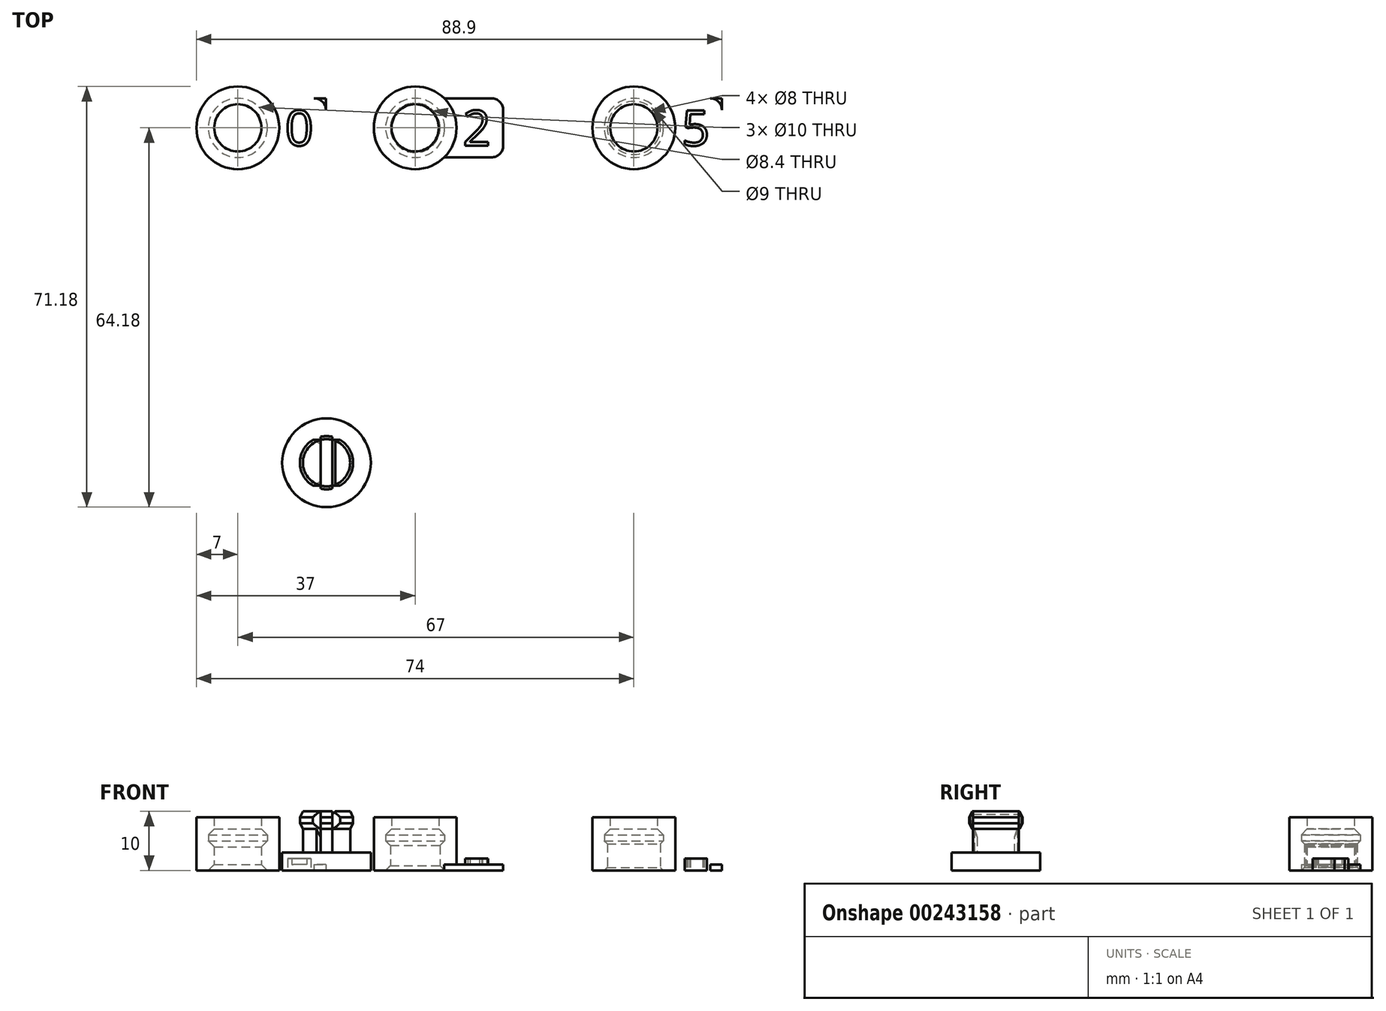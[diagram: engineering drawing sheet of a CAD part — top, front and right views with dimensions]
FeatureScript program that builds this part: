
annotation { "Feature Type Name" : "Feature", "Feature Type Description" : "" }
export const myFeature = defineFeature(function(context is Context, id is Id, definition is map)
    precondition{}
    {
        {
            var Q0;
            Q0=qCreatedBy(makeId("Front.planeOp"),FACE);
            var sketch = newSketch(context, id + "F0", { "sketchPlane" : qUnion([Q0])});
            skLineSegment(sketch, "E0", {"start": v(0, 0) * mm, "end": v(0, 7) * mm, "construction": true});
            skLineSegment(sketch, "E1", {"start": v(0, 7) * mm, "end": v(0, 9) * mm, "construction": true});
            skLineSegment(sketch, "E2", {"start": v(0, 9) * mm, "end": v(-4, 9) * mm, "construction": true});
            skLineSegment(sketch, "E3", {"start": v(0, 0) * mm, "end": v(-4, 0) * mm, "construction": true});
            skLineSegment(sketch, "E4", {"start": v(-4, 9) * mm, "end": v(-4, 7) * mm});
            skLineSegment(sketch, "E5", {"start": v(-4, 7) * mm, "end": v(-5, 6) * mm});
            skLineSegment(sketch, "E6", {"start": v(-5, 6) * mm, "end": v(-5, 5) * mm});
            skLineSegment(sketch, "E7", {"start": v(-5, 5) * mm, "end": v(-4, 4) * mm});
            skLineSegment(sketch, "E8", {"start": v(-4, 4) * mm, "end": v(-4, 0) * mm});
            skLineSegment(sketch, "E9", {"start": v(-4, 0) * mm, "end": v(-7, 0) * mm});
            skLineSegment(sketch, "E10", {"start": v(-7, 0) * mm, "end": v(-7, 9) * mm});
            skLineSegment(sketch, "E11", {"start": v(-7, 9) * mm, "end": v(-4, 9) * mm});
            skLineSegment(sketch, "E12", {"start": v(-4, 1) * mm, "end": v(-5, 0) * mm});
            skLineSegment(sketch, "E13", {"start": v(30, 0) * mm, "end": v(30, 7) * mm, "construction": true});
            skLineSegment(sketch, "E14", {"start": v(30, 7) * mm, "end": v(30, 9) * mm, "construction": true});
            skLineSegment(sketch, "E15", {"start": v(30, 9) * mm, "end": v(26, 9) * mm, "construction": true});
            skLineSegment(sketch, "E16", {"start": v(30, 0) * mm, "end": v(25.8, 0) * mm, "construction": true});
            skLineSegment(sketch, "E17", {"start": v(26, 9) * mm, "end": v(26, 7) * mm});
            skLineSegment(sketch, "E18", {"start": v(26, 7) * mm, "end": v(25, 6) * mm});
            skLineSegment(sketch, "E19", {"start": v(25, 6) * mm, "end": v(25, 5) * mm});
            skLineSegment(sketch, "E20", {"start": v(25, 5) * mm, "end": v(25.8, 4.2) * mm});
            skLineSegment(sketch, "E21", {"start": v(25.8, 4.2) * mm, "end": v(25.8, 0) * mm});
            skLineSegment(sketch, "E22", {"start": v(25.8, 0) * mm, "end": v(23, 0) * mm});
            skLineSegment(sketch, "E23", {"start": v(23, 0) * mm, "end": v(23, 9) * mm});
            skLineSegment(sketch, "E24", {"start": v(23, 9) * mm, "end": v(26, 9) * mm});
            skLineSegment(sketch, "E25", {"start": v(25.8, 0.8) * mm, "end": v(25, 0) * mm});
            skLineSegment(sketch, "E26", {"start": v(67, 0) * mm, "end": v(67, 7) * mm, "construction": true});
            skLineSegment(sketch, "E27", {"start": v(67, 7) * mm, "end": v(67, 9) * mm, "construction": true});
            skLineSegment(sketch, "E28", {"start": v(67, 9) * mm, "end": v(63, 9) * mm, "construction": true});
            skLineSegment(sketch, "E29", {"start": v(67, 0) * mm, "end": v(62.5, 0) * mm, "construction": true});
            skLineSegment(sketch, "E30", {"start": v(63, 9) * mm, "end": v(63, 7) * mm});
            skLineSegment(sketch, "E31", {"start": v(63, 7) * mm, "end": v(62, 6) * mm});
            skLineSegment(sketch, "E32", {"start": v(62, 6) * mm, "end": v(62, 5) * mm});
            skLineSegment(sketch, "E33", {"start": v(62, 5) * mm, "end": v(62.5, 4.5) * mm});
            skLineSegment(sketch, "E34", {"start": v(62.5, 4.5) * mm, "end": v(62.5, 0) * mm});
            skLineSegment(sketch, "E35", {"start": v(62.5, 0) * mm, "end": v(60, 0) * mm});
            skLineSegment(sketch, "E36", {"start": v(60, 0) * mm, "end": v(60, 9) * mm});
            skLineSegment(sketch, "E37", {"start": v(60, 9) * mm, "end": v(63, 9) * mm});
            skLineSegment(sketch, "E38", {"start": v(62.5, 0.5) * mm, "end": v(62, 0) * mm});
            skSolve(sketch);
        }
        {
            var Q0;
            Q0=makeQuery(id+"F0.imprint","IMPRINT",FACE,{"disambiguationData":[TD([[makeQuery(id+"F0.imprint","IMPRINT",EDGE,{"derivedFrom":sQuery(id+"F0.wireOp",EDGE,"E4")}),-1.0]])]});
            var Q1;
            Q1=sQuery(id+"F0.wireOp",EDGE,"E0");
            revolve(context, id + "F1", {"entities" : qUnion([Q0]), "axis" : qUnion([Q1]), "revolveType" : RevolveType.FULL});
        }
        {
            var Q0;
            Q0=makeQuery(id+"F0.imprint","IMPRINT",FACE,{"disambiguationData":[TD([[makeQuery(id+"F0.imprint","IMPRINT",EDGE,{"derivedFrom":sQuery(id+"F0.wireOp",EDGE,"E17")}),-1.0]])]});
            var Q1;
            Q1=sQuery(id+"F0.wireOp",EDGE,"E13");
            revolve(context, id + "F2", {"entities" : qUnion([Q0]), "axis" : qUnion([Q1]), "revolveType" : RevolveType.FULL});
        }
        {
            var Q0;
            Q0=makeQuery(id+"F0.imprint","IMPRINT",FACE,{"disambiguationData":[TD([[makeQuery(id+"F0.imprint","IMPRINT",EDGE,{"derivedFrom":sQuery(id+"F0.wireOp",EDGE,"E30")}),-1.0]])]});
            var Q1;
            Q1=sQuery(id+"F0.wireOp",EDGE,"E26");
            revolve(context, id + "F3", {"entities" : qUnion([Q0]), "axis" : qUnion([Q1]), "revolveType" : RevolveType.FULL});
        }
        {
            var Q0;
            Q0=qCreatedBy(makeId("Top.planeOp"),FACE);
            var sketch = newSketch(context, id + "F4", { "sketchPlane" : qUnion([Q0])});
            skCircle(sketch, "E39.0", {"center": v(0, 0) * mm, "radius": 7 * mm});
            skCircle(sketch, "E40.0", {"center": v(30, 0) * mm, "radius": 7 * mm});
            skCircle(sketch, "E41.0", {"center": v(67, 0) * mm, "radius": 7 * mm});
            skLineSegment(sketch, "E42.bottom", {"start": v(4.9, 5) * mm, "end": v(14.9, 5) * mm});
            skLineSegment(sketch, "E42.top", {"start": v(4.9, -5) * mm, "end": v(14.9, -5) * mm});
            skLineSegment(sketch, "E42.left", {"start": v(4.9, 5) * mm, "end": v(4.9, -5) * mm, "construction": true});
            skLineSegment(sketch, "E42.right", {"start": v(14.9, 5) * mm, "end": v(14.9, -5) * mm});
            skLineSegment(sketch, "E43", {"start": v(0, 0) * mm, "end": v(67, 0) * mm, "construction": true});
            skLineSegment(sketch, "E44.bottom", {"start": v(34.9, 5) * mm, "end": v(44.9, 5) * mm});
            skLineSegment(sketch, "E44.top", {"start": v(34.9, -5) * mm, "end": v(44.9, -5) * mm});
            skLineSegment(sketch, "E44.left", {"start": v(34.9, 5) * mm, "end": v(34.9, -5) * mm, "construction": true});
            skLineSegment(sketch, "E44.right", {"start": v(44.9, 5) * mm, "end": v(44.9, -5) * mm});
            skLineSegment(sketch, "E45.bottom", {"start": v(71.9, 5) * mm, "end": v(81.9, 5) * mm});
            skLineSegment(sketch, "E45.top", {"start": v(71.9, -5) * mm, "end": v(81.9, -5) * mm});
            skLineSegment(sketch, "E45.left", {"start": v(71.9, 5) * mm, "end": v(71.9, -5) * mm, "construction": true});
            skLineSegment(sketch, "E45.right", {"start": v(81.9, 5) * mm, "end": v(81.9, -5) * mm});
            skArc(sketch, "E46", {"start": v(12.9, 5) * mm, "mid": v(14.31, 4.41) * mm, "end": v(14.9, 3) * mm});
            skArc(sketch, "E47", {"start": v(14.9, -3) * mm, "mid": v(14.31, -4.41) * mm, "end": v(12.9, -5) * mm});
            skArc(sketch, "E48", {"start": v(42.9, -5) * mm, "mid": v(44.31, -4.41) * mm, "end": v(44.9, -3) * mm});
            skArc(sketch, "E49", {"start": v(42.9, 5) * mm, "mid": v(44.31, 4.41) * mm, "end": v(44.9, 3) * mm});
            skArc(sketch, "E50", {"start": v(79.9, 5) * mm, "mid": v(81.31, 4.41) * mm, "end": v(81.9, 3) * mm});
            skArc(sketch, "E51", {"start": v(81.9, -3) * mm, "mid": v(81.31, -4.41) * mm, "end": v(79.9, -5) * mm});
            skText(sketch, "E52", { "text": "0", "fontName": "OpenSans-Regular.ttf"});
            skText(sketch, "E53", { "text": "2", "fontName": "OpenSans-Regular.ttf"});
            skText(sketch, "E54", { "text": "5", "fontName": "OpenSans-Regular.ttf"});
            const initialGuessF4  = {"E52": [0.008, -0.003, 1, 0, 0.006], "E53": [0.03804, -0.003, 1, 0, 0.006], "E54": [0.07507, -0.003, 1, 0, 0.006]};
            skSetInitialGuess(sketch, initialGuessF4);
            skSolve(sketch);
        }
        {
            var Q0;
            {var subQ6=sQuery(id+"F4.wireOp",EDGE,"E46");Q0=makeQuery(id+"F4.imprint","IMPRINT",FACE,{"disambiguationData":[TD([[makeQuery(id+"F4.imprint","IMPRINT",EDGE,{"derivedFrom":subQ6}),-1.0]])]});}
            var Q1;
            Q1=makeQuery(id+"F4.imprint","IMPRINT",FACE,{"disambiguationData":[TD([[makeQuery(id+"F4.imprint","IMPRINT",EDGE,{"derivedFrom":sQuery(id+"F4.wireOp",EDGE,"E52.sketch_text.stroke-0")}),-1.0]])]});
            var Q2;
            Q2=makeQuery(id+"F4.imprint","IMPRINT",FACE,{"disambiguationData":[TD([[makeQuery(id+"F4.imprint","IMPRINT",EDGE,{"derivedFrom":sQuery(id+"F4.wireOp",EDGE,"E52.sketch_text.stroke-8")}),1.0]])]});
            extrude(context, id + "F5", {"entities" : qUnion([Q0, Q1, Q2]), "operationType" : NewBodyOperationType.ADD, "depth" : 1 * mm});
        }
        {
            var Q0;
            {var subQ3=sQuery(id+"F4.wireOp",EDGE,"E48");Q0=makeQuery(id+"F4.imprint","IMPRINT",FACE,{"disambiguationData":[TD([[makeQuery(id+"F4.imprint","IMPRINT",EDGE,{"derivedFrom":subQ3}),1.0]])]});}
            var Q1;
            Q1=makeQuery(id+"F4.imprint","IMPRINT",FACE,{"disambiguationData":[TD([[makeQuery(id+"F4.imprint","IMPRINT",EDGE,{"derivedFrom":sQuery(id+"F4.wireOp",EDGE,"E53.sketch_text.stroke-0")}),-1.0]])]});
            extrude(context, id + "F6", {"entities" : qUnion([Q0, Q1]), "operationType" : NewBodyOperationType.ADD, "depth" : 1 * mm});
        }
        {
            var Q0;
            {var subQ0=sQuery(id+"F4.wireOp",EDGE,"E50");Q0=makeQuery(id+"F4.imprint","IMPRINT",FACE,{"disambiguationData":[TD([[makeQuery(id+"F4.imprint","IMPRINT",EDGE,{"derivedFrom":subQ0}),-1.0]])]});}
            var Q1;
            Q1=makeQuery(id+"F4.imprint","IMPRINT",FACE,{"disambiguationData":[TD([[makeQuery(id+"F4.imprint","IMPRINT",EDGE,{"derivedFrom":sQuery(id+"F4.wireOp",EDGE,"E54.sketch_text.stroke-0")}),-1.0]])]});
            extrude(context, id + "F7", {"entities" : qUnion([Q0, Q1]), "operationType" : NewBodyOperationType.ADD, "depth" : 1 * mm});
        }
        {
            var Q0;
            Q0=makeQuery(id+"F4.imprint","IMPRINT",FACE,{"disambiguationData":[TD([[makeQuery(id+"F4.imprint","IMPRINT",EDGE,{"derivedFrom":sQuery(id+"F4.wireOp",EDGE,"E52.sketch_text.stroke-0")}),-1.0]])]});
            extrude(context, id + "F8", {"entities" : qUnion([Q0]), "operationType" : NewBodyOperationType.ADD, "depth" : 2 * mm});
        }
        {
            var Q0;
            Q0=makeQuery(id+"F4.imprint","IMPRINT",FACE,{"disambiguationData":[TD([[makeQuery(id+"F4.imprint","IMPRINT",EDGE,{"derivedFrom":sQuery(id+"F4.wireOp",EDGE,"E53.sketch_text.stroke-0")}),-1.0]])]});
            extrude(context, id + "F9", {"entities" : qUnion([Q0]), "operationType" : NewBodyOperationType.ADD, "depth" : 2 * mm});
        }
        {
            var Q0;
            Q0=makeQuery(id+"F4.imprint","IMPRINT",FACE,{"disambiguationData":[TD([[makeQuery(id+"F4.imprint","IMPRINT",EDGE,{"derivedFrom":sQuery(id+"F4.wireOp",EDGE,"E54.sketch_text.stroke-0")}),-1.0]])]});
            extrude(context, id + "F10", {"entities" : qUnion([Q0]), "operationType" : NewBodyOperationType.ADD, "depth" : 2 * mm});
        }
        {
            var Q0;
            Q0=qCreatedBy(makeId("Top.planeOp"),FACE);
            var sketch = newSketch(context, id + "F11", { "sketchPlane" : qUnion([Q0])});
            skLineSegment(sketch, "E55", {"start": v(0, -30.7) * mm, "end": v(30, -30.7) * mm, "construction": true});
            skLineSegment(sketch, "E56", {"start": v(30, -30.7) * mm, "end": v(15, -56.68) * mm, "construction": true});
            skLineSegment(sketch, "E57", {"start": v(15, -56.68) * mm, "end": v(0, -30.7) * mm, "construction": true});
            skLineSegment(sketch, "E58", {"start": v(0, -56.68) * mm, "end": v(30, -56.68) * mm, "construction": true});
            skLineSegment(sketch, "E59", {"start": v(15, -30.7) * mm, "end": v(15, -82.66) * mm, "construction": true});
            skSolve(sketch);
        }
        {
            var Q0;
            Q0=sQuery(id+"F11.wireOp",EDGE,"E58");
            cPoint(context, id + "F12", {"entities" : qUnion([Q0]), "parameter" : 0.5});
        }
        {
            var Q0;
            Q0 = qCreatedBy(id + "F12" ,VERTEX);
            var Q1;
            Q1=sQuery(id+"F11.wireOp",EDGE,"E58");
            cPlane(context, id + "F13", {"entities" : qUnion([Q0, Q1]), "cplaneType" : CPlaneType.LINE_POINT, "offset" : 25 * mm, "width" : 150 * mm, "height" : 150 * mm});
        }
        {
            var Q0;
            Q0=qCreatedBy(id+"F13.planeOp",FACE);
            var sketch = newSketch(context, id + "F14", { "sketchPlane" : qUnion([Q0])});
            skPoint(sketch, "E60.0", {"position": v(-56.68, 0) * mm});
            skLineSegment(sketch, "E61", {"start": v(-56.68, 0) * mm, "end": v(-56.68, 10) * mm});
            skLineSegment(sketch, "E62", {"start": v(-56.68, 10) * mm, "end": v(-52.68, 10) * mm});
            skLineSegment(sketch, "E63", {"start": v(-52.68, 10) * mm, "end": v(-52.18, 9) * mm});
            skLineSegment(sketch, "E64", {"start": v(-52.18, 9) * mm, "end": v(-52.18, 8) * mm});
            skLineSegment(sketch, "E65", {"start": v(-52.18, 8) * mm, "end": v(-52.68, 7) * mm});
            skLineSegment(sketch, "E66", {"start": v(-52.68, 7) * mm, "end": v(-52.68, 0) * mm});
            skLineSegment(sketch, "E67", {"start": v(-52.68, 0) * mm, "end": v(-56.68, 0) * mm});
            skLineSegment(sketch, "E68", {"start": v(-52.68, 0) * mm, "end": v(-49.18, 0) * mm});
            skLineSegment(sketch, "E69", {"start": v(-49.18, 0) * mm, "end": v(-49.18, 3) * mm});
            skLineSegment(sketch, "E70", {"start": v(-49.18, 3) * mm, "end": v(-52.68, 3) * mm});
            skSolve(sketch);
        }
        {
            var Q0;
            {var subQ0=sQuery(id+"F14.wireOp",EDGE,"E68");Q0=makeQuery(id+"F14.imprint","IMPRINT",FACE,{"disambiguationData":[TD([[makeQuery(id+"F14.imprint","IMPRINT",EDGE,{"derivedFrom":subQ0}),1.0]])]});}
            var Q1;
            Q1=makeQuery(id+"F14.imprint","IMPRINT",FACE,{"disambiguationData":[TD([[makeQuery(id+"F14.imprint","IMPRINT",EDGE,{"derivedFrom":sQuery(id+"F14.wireOp",EDGE,"E61")}),-1.0]])]});
            var Q2;
            Q2=sQuery(id+"F14.wireOp",EDGE,"E61");
            revolve(context, id + "F15", {"entities" : qUnion([Q0, Q1]), "axis" : qUnion([Q2]), "revolveType" : RevolveType.FULL});
        }
        {
            var Q0;
            Q0=makeQuery(id+"F15.opRevolve","SWEPT_FACE",FACE,{"disambiguationData":[OSD([sQuery(id+"F14.wireOp",EDGE,"E62")])]});
            var sketch = newSketch(context, id + "F16", { "sketchPlane" : qUnion([Q0])});
            skCircle(sketch, "E71.0", {"center": v(15, -56.68) * mm, "radius": 4.5 * mm, "construction": true});
            skCircle(sketch, "E72.0", {"center": v(15, -56.68) * mm, "radius": 4 * mm, "construction": true});
            skLineSegment(sketch, "E73.bottom", {"start": v(14, -52.18) * mm, "end": v(16, -52.18) * mm});
            skLineSegment(sketch, "E73.top", {"start": v(14, -61.18) * mm, "end": v(16, -61.18) * mm});
            skLineSegment(sketch, "E73.left", {"start": v(14, -52.18) * mm, "end": v(14, -61.18) * mm});
            skLineSegment(sketch, "E73.right", {"start": v(16, -52.18) * mm, "end": v(16, -61.18) * mm});
            skLineSegment(sketch, "E74", {"start": v(14, -61.18) * mm, "end": v(16, -52.18) * mm, "construction": true});
            skLineSegment(sketch, "E75.bottom", {"start": v(12.7, -61.18) * mm, "end": v(17.3, -61.18) * mm});
            skLineSegment(sketch, "E75.top", {"start": v(12.7, -60.55) * mm, "end": v(17.3, -60.55) * mm});
            skLineSegment(sketch, "E75.left", {"start": v(12.7, -60.55) * mm, "end": v(12.7, -61.18) * mm});
            skLineSegment(sketch, "E75.right", {"start": v(17.3, -60.55) * mm, "end": v(17.3, -61.18) * mm});
            skPoint(sketch, "E76", {"position": v(15, -61.18) * mm});
            skLineSegment(sketch, "E77.bottom", {"start": v(12.7, -52.18) * mm, "end": v(17.3, -52.18) * mm});
            skLineSegment(sketch, "E77.top", {"start": v(12.7, -52.8) * mm, "end": v(17.3, -52.8) * mm});
            skLineSegment(sketch, "E77.left", {"start": v(12.7, -52.18) * mm, "end": v(12.7, -52.8) * mm});
            skLineSegment(sketch, "E77.right", {"start": v(17.3, -52.18) * mm, "end": v(17.3, -52.8) * mm});
            skPoint(sketch, "E78", {"position": v(15, -52.18) * mm});
            skPoint(sketch, "E79", {"position": v(16, -60.55) * mm});
            skPoint(sketch, "E80", {"position": v(16, -52.8) * mm});
            skSolve(sketch);
        }
        {
            var Q0;
            {var subQ5=sQuery(id+"F16.wireOp",EDGE,"E77.left");Q0=makeQuery(id+"F16.imprint","IMPRINT",FACE,{"disambiguationData":[TD([[makeQuery(id+"F16.imprint","IMPRINT",EDGE,{"derivedFrom":subQ5}),1.0]])]});}
            var Q1;
            {var subQ0=sQuery(id+"F16.wireOp",EDGE,"E77.bottom");var subQ1=sQuery(id+"F16.wireOp",EDGE,"E73.left");var subQ2=makeQuery(id+"F16.imprint","INTERSECT",VERTEX,{"derivedFrom":[subQ1,subQ0]});Q1=makeQuery(id+"F16.imprint","IMPRINT",FACE,{"disambiguationData":[TD([[makeQuery(id+"F16.imprint","IMPRINT",EDGE,{"disambiguationData":[TD([[subQ2,-1.0]])],"derivedFrom":subQ0}),-1.0]])]});}
            var Q2;
            {var subQ5=sQuery(id+"F16.wireOp",EDGE,"E77.right");Q2=makeQuery(id+"F16.imprint","IMPRINT",FACE,{"disambiguationData":[TD([[makeQuery(id+"F16.imprint","IMPRINT",EDGE,{"derivedFrom":subQ5}),-1.0]])]});}
            var Q3;
            {var subQ0=sQuery(id+"F16.wireOp",EDGE,"E77.top");var subQ1=makeQuery(id+"F15.opRevolve","SWEPT_EDGE",EDGE,{"disambiguationData":[OSD([sQuery(id+"F14.wireOp",EDGE,"E62"),sQuery(id+"F14.wireOp",EDGE,"E63")])]});var subQ2=makeQuery(id+"F16.imprint","INTERSECT",VERTEX,{"derivedFrom":[subQ1,sQuery(id+"F16.wireOp",EDGE,"E73.left"),subQ0]});Q3=makeQuery(id+"F16.imprint","IMPRINT",FACE,{"disambiguationData":[TD([[makeQuery(id+"F16.imprint","IMPRINT",EDGE,{"disambiguationData":[TD([[subQ2,-1.0]])],"derivedFrom":subQ0}),1.0]])]});}
            var Q4;
            {var subQ0=sQuery(id+"F16.wireOp",EDGE,"E77.top");var subQ1=sQuery(id+"F16.wireOp",EDGE,"E73.left");var subQ2=makeQuery(id+"F15.opRevolve","SWEPT_EDGE",EDGE,{"disambiguationData":[OSD([sQuery(id+"F14.wireOp",EDGE,"E62"),sQuery(id+"F14.wireOp",EDGE,"E63")])]});var subQ3=makeQuery(id+"F16.imprint","INTERSECT",VERTEX,{"derivedFrom":[subQ2,subQ1,subQ0]});Q4=makeQuery(id+"F16.imprint","IMPRINT",FACE,{"disambiguationData":[TD([[makeQuery(id+"F16.imprint","IMPRINT",EDGE,{"disambiguationData":[TD([[subQ3,-1.0]])],"derivedFrom":subQ1}),1.0]])]});}
            var Q5;
            {var subQ0=sQuery(id+"F16.wireOp",EDGE,"E75.top");var subQ1=makeQuery(id+"F15.opRevolve","SWEPT_EDGE",EDGE,{"disambiguationData":[OSD([sQuery(id+"F14.wireOp",EDGE,"E62"),sQuery(id+"F14.wireOp",EDGE,"E63")])]});var subQ2=makeQuery(id+"F16.imprint","INTERSECT",VERTEX,{"derivedFrom":[subQ1,sQuery(id+"F16.wireOp",EDGE,"E73.left"),subQ0]});Q5=makeQuery(id+"F16.imprint","IMPRINT",FACE,{"disambiguationData":[TD([[makeQuery(id+"F16.imprint","IMPRINT",EDGE,{"disambiguationData":[TD([[subQ2,-1.0]])],"derivedFrom":subQ0}),-1.0]])]});}
            var Q6;
            {var subQ5=sQuery(id+"F16.wireOp",EDGE,"E75.right");Q6=makeQuery(id+"F16.imprint","IMPRINT",FACE,{"disambiguationData":[TD([[makeQuery(id+"F16.imprint","IMPRINT",EDGE,{"derivedFrom":subQ5}),-1.0]])]});}
            var Q7;
            {var subQ0=sQuery(id+"F16.wireOp",EDGE,"E75.bottom");var subQ1=sQuery(id+"F16.wireOp",EDGE,"E73.left");var subQ2=makeQuery(id+"F16.imprint","INTERSECT",VERTEX,{"derivedFrom":[subQ1,subQ0]});Q7=makeQuery(id+"F16.imprint","IMPRINT",FACE,{"disambiguationData":[TD([[makeQuery(id+"F16.imprint","IMPRINT",EDGE,{"disambiguationData":[TD([[subQ2,-1.0]])],"derivedFrom":subQ0}),1.0]])]});}
            var Q8;
            {var subQ5=sQuery(id+"F16.wireOp",EDGE,"E75.left");Q8=makeQuery(id+"F16.imprint","IMPRINT",FACE,{"disambiguationData":[TD([[makeQuery(id+"F16.imprint","IMPRINT",EDGE,{"derivedFrom":subQ5}),1.0]])]});}
            var Q9;
            Q9=makeQuery(id+"F15.opRevolve","SWEPT_FACE",FACE,{"disambiguationData":[OSD([sQuery(id+"F14.wireOp",EDGE,"E70")])]});
            extrude(context, id + "F17", {"entities" : qUnion([Q0, Q1, Q2, Q3, Q4, Q5, Q6, Q7, Q8]), "operationType" : NewBodyOperationType.REMOVE, "endBound" : BoundingType.UP_TO_SURFACE, "oppositeDirection" : true, "endBoundEntityFace" : qUnion([Q9]), "depth" : 25 * mm});
        }
        {
            var Q0;
            {var subQ0=sQuery(id+"F14.wireOp",EDGE,"E63");var subQ1=sQuery(id+"F14.wireOp",EDGE,"E62");var subQ2=sQuery(id+"F16.wireOp",EDGE,"E73.left");var subQ3=sQuery(id+"F16.wireOp",EDGE,"E75.top");Q0=makeQuery(id+"F17.boolean.opBoolean","COPY",EDGE,{"disambiguationData":[TD([makeQuery(id+"F15.opRevolve","SWEPT_FACE",FACE,{"disambiguationData":[OSD([subQ1])]})])],"derivedFrom":makeQuery(id+"F17.opExtrude","SWEPT_EDGE",EDGE,{"disambiguationData":[OSD([subQ1,subQ0,subQ2,subQ3])]})});}
            var Q1;
            Q1=makeQuery(id+"F17.boolean.opBoolean","COPY",EDGE,{"derivedFrom":makeQuery(id+"F17.opExtrude","CAP_EDGE",EDGE,{"disambiguationData":[OSD([sQuery(id+"F16.wireOp",EDGE,"E73.left")])],"isStart":true})});
            var Q2;
            {var subQ0=sQuery(id+"F16.wireOp",EDGE,"E75.top");var subQ1=sQuery(id+"F16.wireOp",EDGE,"E73.right");var subQ2=sQuery(id+"F14.wireOp",EDGE,"E63");var subQ3=sQuery(id+"F14.wireOp",EDGE,"E62");Q2=makeQuery(id+"F17.boolean.opBoolean","COPY",EDGE,{"disambiguationData":[TD([makeQuery(id+"F15.opRevolve","SWEPT_FACE",FACE,{"disambiguationData":[OSD([subQ3])]})])],"derivedFrom":makeQuery(id+"F17.opExtrude","SWEPT_EDGE",EDGE,{"disambiguationData":[OSD([subQ3,subQ2,subQ1,subQ0])]})});}
            var Q3;
            Q3=makeQuery(id+"F17.boolean.opBoolean","COPY",EDGE,{"derivedFrom":makeQuery(id+"F17.opExtrude","CAP_EDGE",EDGE,{"disambiguationData":[OSD([sQuery(id+"F16.wireOp",EDGE,"E73.right")])],"isStart":true})});
            var Q4;
            {var subQ0=sQuery(id+"F14.wireOp",EDGE,"E63");var subQ1=sQuery(id+"F14.wireOp",EDGE,"E62");var subQ2=sQuery(id+"F16.wireOp",EDGE,"E73.left");var subQ3=sQuery(id+"F16.wireOp",EDGE,"E77.top");Q4=makeQuery(id+"F17.boolean.opBoolean","COPY",EDGE,{"disambiguationData":[TD([makeQuery(id+"F15.opRevolve","SWEPT_FACE",FACE,{"disambiguationData":[OSD([subQ1])]})])],"derivedFrom":makeQuery(id+"F17.opExtrude","SWEPT_EDGE",EDGE,{"disambiguationData":[OSD([subQ1,subQ0,subQ2,subQ3])]})});}
            var Q5;
            {var subQ0=sQuery(id+"F14.wireOp",EDGE,"E63");var subQ1=sQuery(id+"F14.wireOp",EDGE,"E62");var subQ2=sQuery(id+"F16.wireOp",EDGE,"E73.right");var subQ3=sQuery(id+"F16.wireOp",EDGE,"E77.top");Q5=makeQuery(id+"F17.boolean.opBoolean","COPY",EDGE,{"disambiguationData":[TD([makeQuery(id+"F15.opRevolve","SWEPT_FACE",FACE,{"disambiguationData":[OSD([subQ1])]})])],"derivedFrom":makeQuery(id+"F17.opExtrude","SWEPT_EDGE",EDGE,{"disambiguationData":[OSD([subQ1,subQ0,subQ2,subQ3])]})});}
            chamfer(context, id + "F18", {"entities" : qUnion([Q0, Q1, Q2, Q3, Q4, Q5]), "width" : .5 * mm, "tangentPropagation" : true});
        }
    });
